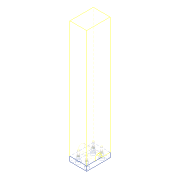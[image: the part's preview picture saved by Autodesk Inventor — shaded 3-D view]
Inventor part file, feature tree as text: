
AUTODESK INVENTOR PART (.ipt)
format: ipt  version: 2018 (Build 220112000, 112)  size: 143,360 bytes
history: native  units: mm
features: other x4, sketch x2, extrude x1, chamfer x1, hole x1
ambient origin geometry x8: Origin, YZ Plane, XZ Plane, XY Plane, X Axis, Y Axis, Z Axis, Center Point
bodies: Solid1 (feature_tree)
feature tree (9):
  other  "10-002-ARM.ipt"
  extrude  "Extrusion1"  Depth=15.0mm TaperAngle=0.0deg
  chamfer  "Chamfer1"  Distance=3.0mm Angle=45.0deg
  hole  "Hole1"  [1 undecoded]
  other  "TaggingFeature1"
  sketch  "Sketch1"  dims[d0=10.0mm d1=15.0mm d2=0.0mm d3=3.0mm d4=2.0mm d5=45.0deg]
  sketch  "Sketch2"  dims[d6=5.5mm d7=6.0mm d8=10.0mm d9=5.4mm d10=90.0deg d11=8.0mm d12=20.594885mm]
  other  "Solid1::10-002-ARM.ipt"
  other  "Srf1"
note: 1 required parameter value undecoded (feature->parameter linkage not recoverable at this tier; creation-order binding heuristic only, values carry confidence <= 0.55)
